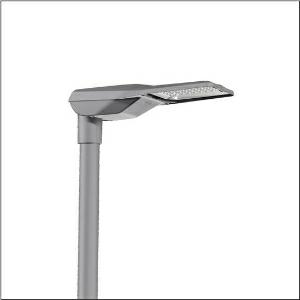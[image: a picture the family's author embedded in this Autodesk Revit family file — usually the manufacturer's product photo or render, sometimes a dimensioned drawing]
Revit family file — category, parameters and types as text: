
# Revit family: streetlight_sl_21_iq_mini___st0_8a_5xe2c31d08gb_9b37
name_source: partatom
category: Lighting Fixtures
units: mm (PartAtom-declared; Revit-internal decimal feet)

## family parameters
Cut with Voids When Loaded = No
Host = Face
Light Source = No
Part Type = Normal
Room Calculation Point = No
Round Connector Dimension = Use Diameter
Shared = No

## types (1)
- --- (1 x LED, 5680 lm, 37.1 W, 3000K)
    Apparent Load = 37 VA
    CIE Flux Codes = 38 75 97 100 100
    Color Rendering = 70
    Color Temperature = 3000K
    Default Elevation = 1800 mm
    Description = Streetlight SL 21 iQ mini, mast luminaire, primary light control with lens, of PMMA, primary optical cover: cover, of toughened safety glass, transparent, light distribution: ST0.8a, light emission: direct distribution, primary light characteristic: asymmetric, installation type: post-top, side-entry, LED, High Power LED, rated luminous flux: 5.680lm, luminous efficacy: 153lm/W, light colour: 730, colour temperature: 3000K, control gear: iQ-Comfort, control: Auto-Match, Temp-Guard, Lumen-Switch, Night-Set, Smart-Wire, Light-Fading, Desk-Remote (wireless, voltage-free reading and setting of iQ features in the workshop via application-optimized NFC function/RFID function), optimised constant luminous flux control (CLO 2.0), pre-setting: linear dimming characteristic, mains connection: 220..240V, AC, 50/60Hz, start of lifetime: 37W, end of service life: 39W, reduction: 18W, luminaire housing, of diecast aluminium, powder-coated, Siteco® metallic grey (DB 702S), corrosivity category C5 mid according to DIN EN ISO 12944, please order mast flange separately, inclination adjustable: 0°, 5°, 10°, 15°, sealing non-destructively replaceable, multi-level sealing system, length: 628mm, width: 235mm, height: 110mm, mast flange for spigot size: 42mm (side-entry): 5XC10008XM4, 60/48mm (side-entry/post-top): 5XC10108XM2, 76/60mm (side-entry/post-top): 5XC10108XM1, mounting height: 4..8m, protection rating (complete): IP66, insulation class (complete): insulation class II (safety insulation), certification: CE, ENEC, ENEC+, VDE, impact resistance: IK10, permissible operating ambient temperature for outdoor applications: -40..+50°C, standard-compliant lighting for roads and squares, packaging unit: 1 piece

Light Distribution: ST0.8a
    Height = 110 mm
    Lamp = 1 x LED
    Lamp Light Flux = 5680 lm
    Lamp Power = 37.1 W
    Lamp count = 1
    Length = 625 mm
    Luminous efficacy = 153 lm/W
    Manufacturer = Siteco
    ModVariant = No
    Model = 5XE2C31D08GB
    Number of Poles = 1
    OnlyDefault = Yes
    Power Factor = 1
    Product Name = Streetlight SL 21 iQ mini | ST0.8a
    Product group = mast luminaire | pylon top
    ProductGroupID = 6100
    Protection Class = Protection class II
    Protection Degree = IP 66
    RLX_Detail_Level = 1
    RLX_Emergency_Light_Flux = 0 lm
    RLX_Emergency_Type = 0
    RLX_Emergency_Type_DB = No
    RlxData = <blob elided: 26369 chars, md5=82840b3e>
    Socket = socket
    Standby Power = 0 W
    System Light Flux = 5680 lm
    System Power = 37 W
    Type Comments = factory setting: luminous flux: 100 % | dim-lin: 254 | 385 mA
    Type Image = l_1003519.jpg
    URL = http://relux.com
    VarID = @adj_207017
    Voltage = 0 V
    Weight = 0.00 kg
    Width = 234 mm

## geometry (parser evidence)
native form markers: Blend x4, Sweep x10
no freeform markers — native parametric forms only
